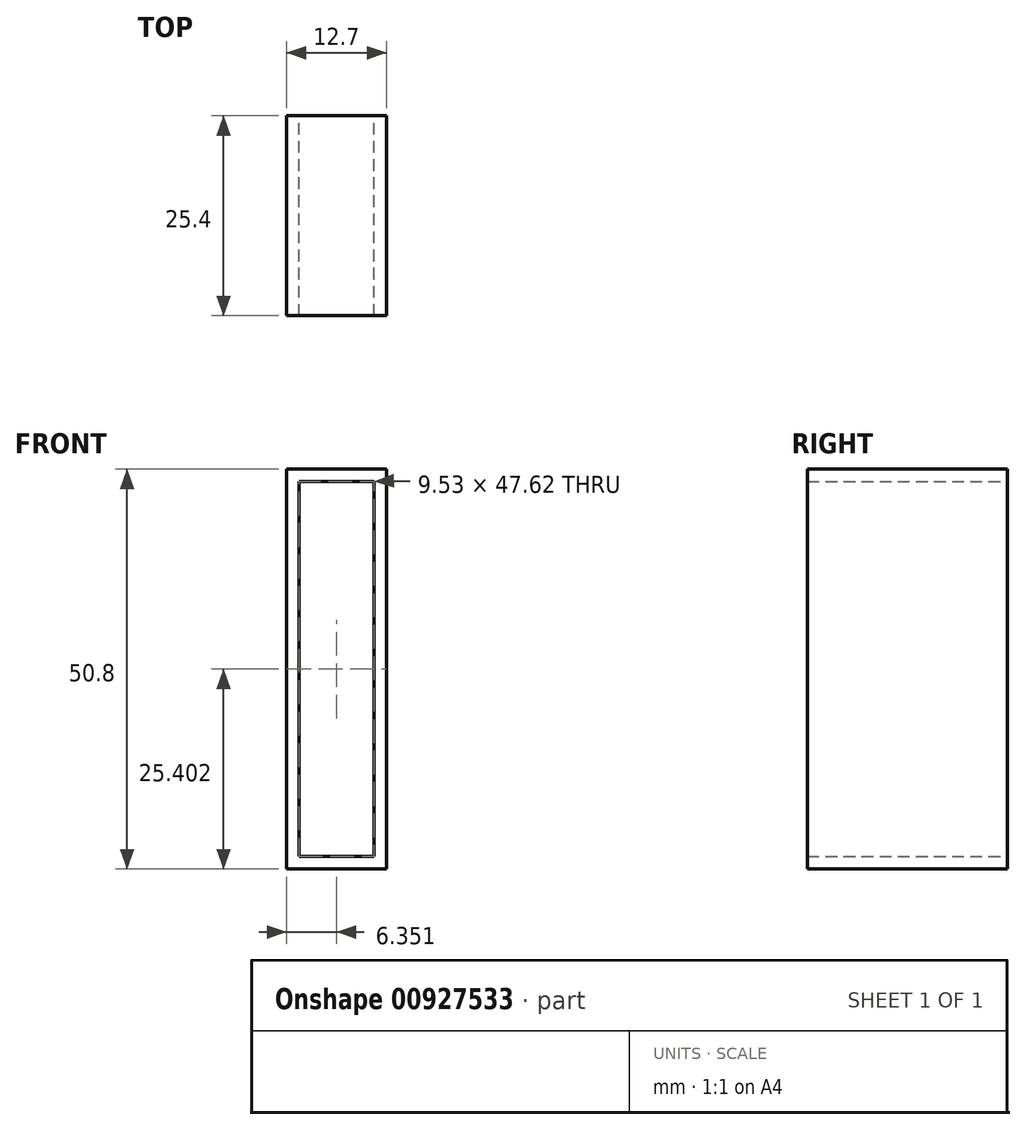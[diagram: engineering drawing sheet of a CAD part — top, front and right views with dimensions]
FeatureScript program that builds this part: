
annotation { "Feature Type Name" : "Feature", "Feature Type Description" : "" }
export const myFeature = defineFeature(function(context is Context, id is Id, definition is map)
    precondition{}
    {
        {
            var Q0;
            Q0=qCreatedBy(makeId("Front.planeOp"),FACE);
            var sketch = newSketch(context, id + "F0", { "sketchPlane" : qUnion([Q0])});
            skLineSegment(sketch, "E0.bottom", {"start": v(-34.42, 37.48) * mm, "end": v(-21.72, 37.48) * mm});
            skLineSegment(sketch, "E0.top", {"start": v(-34.42, -13.32) * mm, "end": v(-21.72, -13.32) * mm});
            skLineSegment(sketch, "E0.left", {"start": v(-34.42, 37.48) * mm, "end": v(-34.42, -13.32) * mm});
            skLineSegment(sketch, "E0.right", {"start": v(-21.72, 37.48) * mm, "end": v(-21.72, -13.32) * mm});
            skLineSegment(sketch, "E1.bottom", {"start": v(-32.83, 35.9) * mm, "end": v(-23.3, 35.9) * mm});
            skLineSegment(sketch, "E1.top", {"start": v(-32.83, -11.73) * mm, "end": v(-23.3, -11.73) * mm});
            skLineSegment(sketch, "E1.left", {"start": v(-32.83, 35.9) * mm, "end": v(-32.83, -11.73) * mm});
            skLineSegment(sketch, "E1.right", {"start": v(-23.3, 35.9) * mm, "end": v(-23.3, -11.73) * mm});
            skSolve(sketch);
        }
        {
            var Q0;
            Q0=makeQuery(id+"F0.imprint","IMPRINT",FACE,{"disambiguationData":[TD([[makeQuery(id+"F0.imprint","IMPRINT",EDGE,{"derivedFrom":sQuery(id+"F0.wireOp",EDGE,"E0.bottom")}),-1.0]])]});
            extrude(context, id + "F1", {"entities" : qUnion([Q0]), "depth" : 25.4 * mm, "offsetDistance" : 25.4 * mm});
        }
    });
